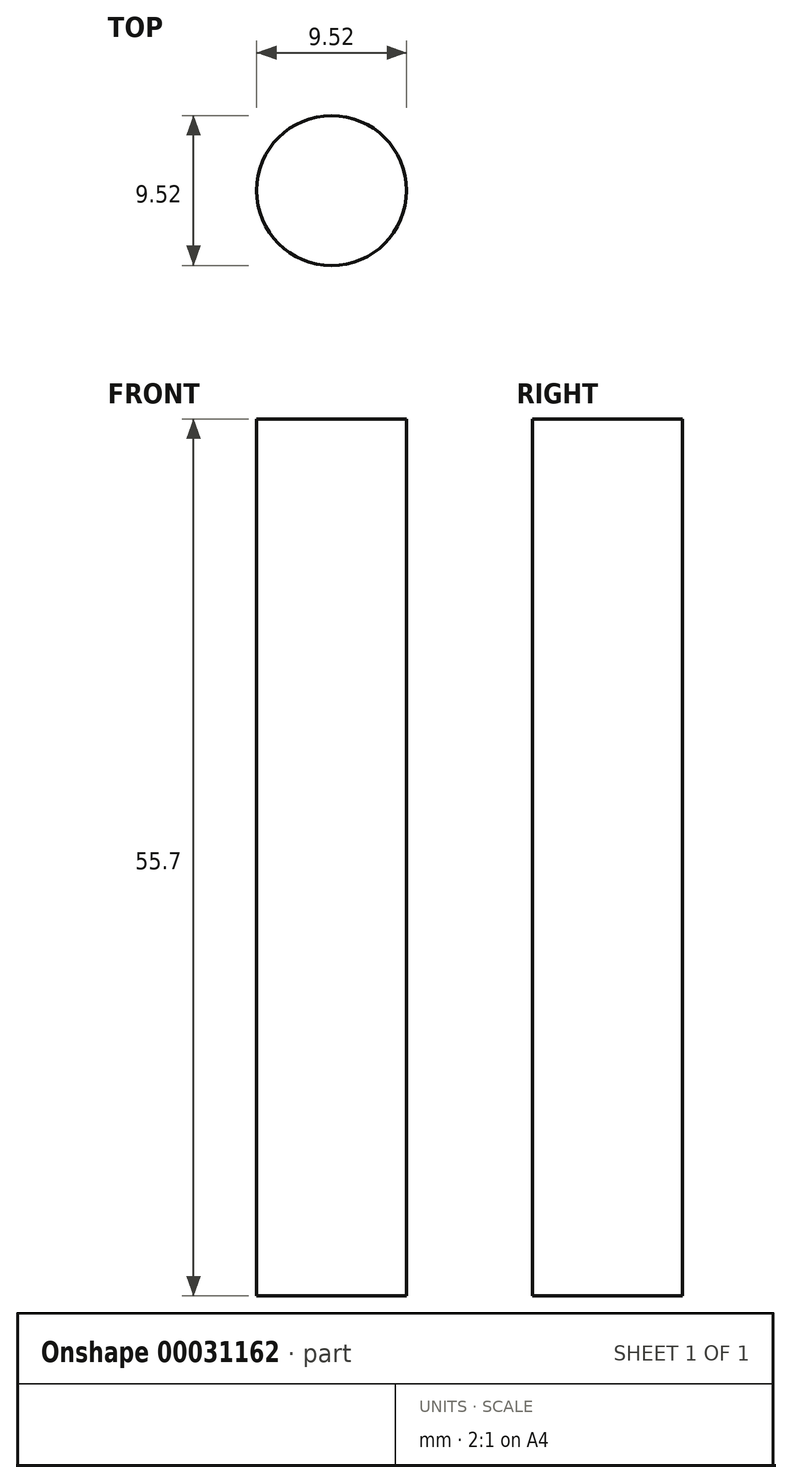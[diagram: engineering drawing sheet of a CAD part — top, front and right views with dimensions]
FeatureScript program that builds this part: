
annotation { "Feature Type Name" : "Feature", "Feature Type Description" : "" }
export const myFeature = defineFeature(function(context is Context, id is Id, definition is map)
    precondition{}
    {
        {
            var Q0;
            Q0=qCreatedBy(makeId("Top.planeOp"),FACE);
            var sketch = newSketch(context, id + "F0", { "sketchPlane" : qUnion([Q0])});
            skCircle(sketch, "E0", {"center": v(0, 0) * mm, "radius": 4.76 * mm});
            skSolve(sketch);
        }
        {
            var Q0;
            Q0 = qSketchRegion(id + "F0", true);
            extrude(context, id + "F1", {"entities" : qUnion([Q0]), "depth" : (20 + 12.7 + 23) * mm});
        }
    });
